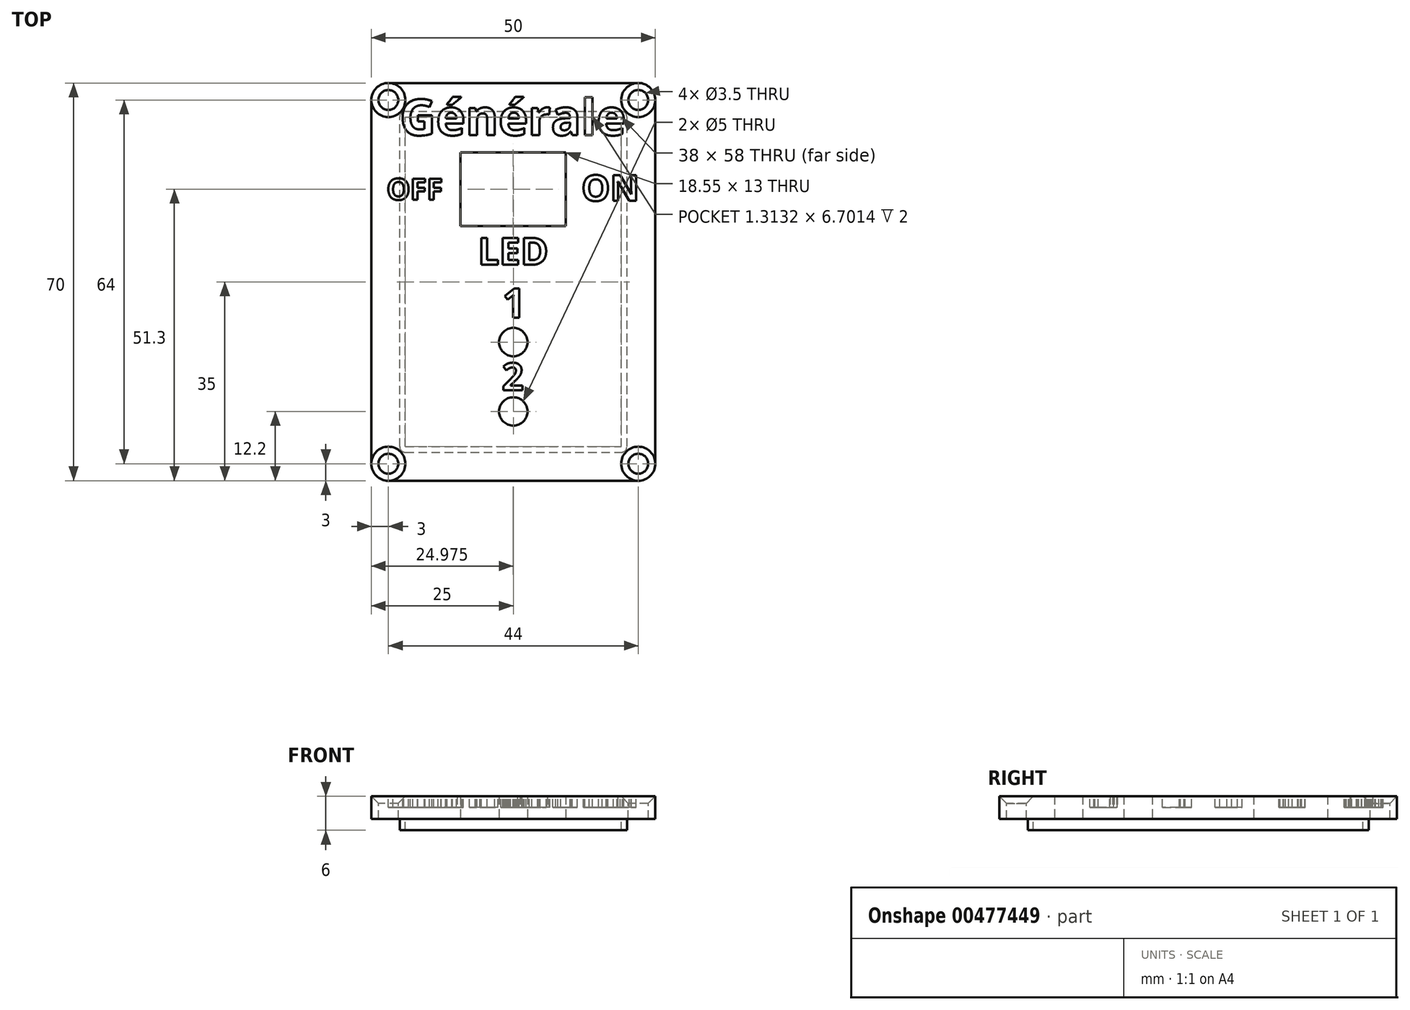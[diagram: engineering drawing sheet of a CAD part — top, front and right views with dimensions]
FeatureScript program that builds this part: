
annotation { "Feature Type Name" : "Feature", "Feature Type Description" : "" }
export const myFeature = defineFeature(function(context is Context, id is Id, definition is map)
    precondition{}
    {
        {
            var Q0;
            Q0=qCreatedBy(makeId("Top.planeOp"),FACE);
            var sketch = newSketch(context, id + "F0", { "sketchPlane" : qUnion([Q0])});
            skLineSegment(sketch, "E0.bottom", {"start": v(-25, 35) * mm, "end": v(25, 35) * mm});
            skLineSegment(sketch, "E0.top", {"start": v(-25, -35) * mm, "end": v(25, -35) * mm});
            skLineSegment(sketch, "E0.left", {"start": v(-25, 35) * mm, "end": v(-25, -35) * mm});
            skLineSegment(sketch, "E0.right", {"start": v(25, 35) * mm, "end": v(25, -35) * mm});
            skLineSegment(sketch, "E1.bottom", {"start": v(-9.3, 22.8) * mm, "end": v(9.25, 22.8) * mm});
            skLineSegment(sketch, "E1.top", {"start": v(-9.3, 9.8) * mm, "end": v(9.25, 9.8) * mm});
            skLineSegment(sketch, "E1.left", {"start": v(-9.3, 22.8) * mm, "end": v(-9.3, 9.8) * mm});
            skLineSegment(sketch, "E1.right", {"start": v(9.25, 22.8) * mm, "end": v(9.25, 9.8) * mm});
            skPoint(sketch, "E2", {"position": v(0, -22.8) * mm});
            skPoint(sketch, "E3", {"position": v(0, -10.6) * mm});
            skSolve(sketch);
        }
        {
            var Q0;
            Q0 = qSketchRegion(id + "F0", true);
            extrude(context, id + "F1", {"entities" : qUnion([Q0]), "depth" : 4 * mm});
        }
        {
            var Q0;
            Q0=sQuery(id+"F0.wireOp",VERTEX,"E3");
            var Q1;
            Q1=sQuery(id+"F0.wireOp",VERTEX,"E2");
            var Q2;
            Q2=makeQuery(id+"F1.opExtrude","SWEPT_BODY",BODY,{"disambiguationData":[OSD([sQuery(id+"F0.wireOp",EDGE,"E0.bottom"),sQuery(id+"F0.wireOp",EDGE,"E0.top"),sQuery(id+"F0.wireOp",EDGE,"E0.left"),sQuery(id+"F0.wireOp",EDGE,"E0.right"),sQuery(id+"F0.wireOp",EDGE,"E1.bottom"),sQuery(id+"F0.wireOp",EDGE,"E1.top"),sQuery(id+"F0.wireOp",EDGE,"E1.left"),sQuery(id+"F0.wireOp",EDGE,"E1.right")])]});
            hole(context, id + "F2", {"style" : HoleStyle.SIMPLE, "endStyle" : HoleEndStyle.THROUGH, "oppositeDirection" : true, "holeDiameter" : 5 * mm, "isTappedThrough" : true, "tappedDepth" : 12.7 * mm, "tapClearance" : 3, "locations" : qUnion([Q0, Q1]), "scope" : qUnion([Q2])});
        }
        {
            var Q0;
            Q0=makeQuery(id+"F1.opExtrude","CAP_FACE",FACE,{"disambiguationData":[OSD([sQuery(id+"F0.wireOp",EDGE,"E0.bottom"),sQuery(id+"F0.wireOp",EDGE,"E0.top"),sQuery(id+"F0.wireOp",EDGE,"E0.left"),sQuery(id+"F0.wireOp",EDGE,"E0.right"),sQuery(id+"F0.wireOp",EDGE,"E1.bottom"),sQuery(id+"F0.wireOp",EDGE,"E1.top"),sQuery(id+"F0.wireOp",EDGE,"E1.left"),sQuery(id+"F0.wireOp",EDGE,"E1.right")])],"isStart":false});
            var sketch = newSketch(context, id + "F3", { "sketchPlane" : qUnion([Q0])});
            skText(sketch, "E4", { "text": "ON", "fontName": "OpenSans-Bold.ttf"});
            skText(sketch, "E5", { "text": "OFF\n", "fontName": "OpenSans-Bold.ttf"});
            skText(sketch, "E6", { "text": "Générale", "fontName": "OpenSans-Bold.ttf"});
            skText(sketch, "E7", { "text": "LED", "fontName": "OpenSans-Bold.ttf"});
            skText(sketch, "E8", { "text": "1", "fontName": "OpenSans-Bold.ttf"});
            skText(sketch, "E9", { "text": "2", "fontName": "OpenSans-Bold.ttf"});
            const initialGuessF3  = {"E4": [0.012, 0.01425, 1, 0, 0.00455], "E5": [-0.0223, 0.01443, 1, 0, 0.00377], "E6": [-0.02, 0.0258, 1, 0, 0.00635], "E7": [-0.00622, 0.003, 1, 0, 0.00478], "E8": [-0.00192, -0.0063, 1, 0, 0.0052], "E9": [-0.00202, -0.01907, 1, 0, 0.00483]};
            skSetInitialGuess(sketch, initialGuessF3);
            skSolve(sketch);
        }
        {
            var Q0;
            Q0 = qSketchRegion(id + "F3", true);
            extrude(context, id + "F4", {"entities" : qUnion([Q0]), "operationType" : NewBodyOperationType.REMOVE, "oppositeDirection" : true, "depth" : 2 * mm});
        }
        {
            var Q0;
            {var subQ0=sQuery(id+"F0.wireOp",EDGE,"E0.bottom");var subQ1=sQuery(id+"F0.wireOp",EDGE,"E0.top");var subQ2=sQuery(id+"F0.wireOp",EDGE,"E0.left");var subQ3=sQuery(id+"F0.wireOp",EDGE,"E0.right");var subQ4=sQuery(id+"F0.wireOp",EDGE,"E1.bottom");var subQ5=sQuery(id+"F0.wireOp",EDGE,"E1.top");var subQ6=sQuery(id+"F0.wireOp",EDGE,"E1.left");var subQ7=sQuery(id+"F0.wireOp",EDGE,"E1.right");Q0=makeQuery(id+"F4.boolean.opBoolean","SPLIT",FACE,{"disambiguationData":[TD([makeQuery(id+"F1.opExtrude","SWEPT_FACE",FACE,{"disambiguationData":[OSD([subQ0])]})])],"derivedFrom":makeQuery(id+"F1.opExtrude","CAP_FACE",FACE,{"disambiguationData":[OSD([subQ0,subQ1,subQ2,subQ3,subQ4,subQ5,subQ6,subQ7])],"isStart":false})});}
            var sketch = newSketch(context, id + "F5", { "sketchPlane" : qUnion([Q0])});
            skPoint(sketch, "E10", {"position": v(-22, 32) * mm});
            skPoint(sketch, "E11", {"position": v(22, 32) * mm});
            skPoint(sketch, "E12", {"position": v(-22, -32) * mm});
            skPoint(sketch, "E13", {"position": v(22, -32) * mm});
            skSolve(sketch);
        }
        {
            var Q0;
            Q0=sQuery(id+"F5.wireOp",VERTEX,"E10");
            var Q1;
            Q1=sQuery(id+"F5.wireOp",VERTEX,"E11");
            var Q2;
            Q2=sQuery(id+"F5.wireOp",VERTEX,"E13");
            var Q3;
            Q3=sQuery(id+"F5.wireOp",VERTEX,"E12");
            var Q4;
            Q4=makeQuery(id+"F1.opExtrude","SWEPT_BODY",BODY,{"disambiguationData":[OSD([sQuery(id+"F0.wireOp",EDGE,"E0.bottom"),sQuery(id+"F0.wireOp",EDGE,"E0.top"),sQuery(id+"F0.wireOp",EDGE,"E0.left"),sQuery(id+"F0.wireOp",EDGE,"E0.right"),sQuery(id+"F0.wireOp",EDGE,"E1.bottom"),sQuery(id+"F0.wireOp",EDGE,"E1.top"),sQuery(id+"F0.wireOp",EDGE,"E1.left"),sQuery(id+"F0.wireOp",EDGE,"E1.right")])]});
            hole(context, id + "F6", {"style" : HoleStyle.C_SINK, "endStyle" : HoleEndStyle.THROUGH, "holeDiameter" : 3.5 * mm, "cSinkDiameter" : 6 * mm, "cSinkAngle" : 90 * degree, "isTappedThrough" : true, "tappedDepth" : 12.7 * mm, "tapClearance" : 3, "locations" : qUnion([Q0, Q1, Q2, Q3]), "scope" : qUnion([Q4])});
        }
        {
            var Q0;
            Q0=makeQuery(id+"F1.opExtrude","SWEPT_EDGE",EDGE,{"disambiguationData":[OSD([sQuery(id+"F0.wireOp",EDGE,"E0.bottom"),sQuery(id+"F0.wireOp",EDGE,"E0.left")])]});
            var Q1;
            Q1=makeQuery(id+"F1.opExtrude","SWEPT_EDGE",EDGE,{"disambiguationData":[OSD([sQuery(id+"F0.wireOp",EDGE,"E0.bottom"),sQuery(id+"F0.wireOp",EDGE,"E0.right")])]});
            var Q2;
            Q2=makeQuery(id+"F1.opExtrude","SWEPT_EDGE",EDGE,{"disambiguationData":[OSD([sQuery(id+"F0.wireOp",EDGE,"E0.top"),sQuery(id+"F0.wireOp",EDGE,"E0.right")])]});
            var Q3;
            Q3=makeQuery(id+"F1.opExtrude","SWEPT_EDGE",EDGE,{"disambiguationData":[OSD([sQuery(id+"F0.wireOp",EDGE,"E0.top"),sQuery(id+"F0.wireOp",EDGE,"E0.left")])]});
            fillet(context, id + "F7", {"entities" : qUnion([Q0, Q1, Q2, Q3]), "radius" : 3 * mm, "tangentPropagation" : true, "allowEdgeOverflow" : false});
        }
        {
            var Q0;
            Q0=makeQuery(id+"F0.imprint","IMPRINT",FACE,{"disambiguationData":[TD([[makeQuery(id+"F0.imprint","IMPRINT",EDGE,{"derivedFrom":sQuery(id+"F0.wireOp",EDGE,"E0.bottom")}),-1.0]])]});
            var sketch = newSketch(context, id + "F8", { "sketchPlane" : qUnion([Q0])});
            skLineSegment(sketch, "E14.bottom", {"start": v(-20, -30) * mm, "end": v(20, -30) * mm});
            skLineSegment(sketch, "E14.top", {"start": v(-20, 30) * mm, "end": v(20, 30) * mm});
            skLineSegment(sketch, "E14.left", {"start": v(-20, -30) * mm, "end": v(-20, 30) * mm});
            skLineSegment(sketch, "E14.right", {"start": v(20, -30) * mm, "end": v(20, 30) * mm});
            skLineSegment(sketch, "E15.bottom", {"start": v(-19, -29) * mm, "end": v(19, -29) * mm});
            skLineSegment(sketch, "E15.top", {"start": v(-19, 29) * mm, "end": v(19, 29) * mm});
            skLineSegment(sketch, "E15.left", {"start": v(-19, -29) * mm, "end": v(-19, 29) * mm});
            skLineSegment(sketch, "E15.right", {"start": v(19, -29) * mm, "end": v(19, 29) * mm});
            skSolve(sketch);
        }
        {
            var Q0;
            Q0=makeQuery(id+"F8.imprint","IMPRINT",FACE,{"disambiguationData":[TD([[makeQuery(id+"F8.imprint","IMPRINT",EDGE,{"derivedFrom":sQuery(id+"F8.wireOp",EDGE,"E14.bottom")}),1.0]])]});
            var Q1;
            Q1=sQuery(id+"F8.wireOp",EDGE,"E15.bottom");
            var Q2;
            Q2=sQuery(id+"F8.wireOp",EDGE,"E14.bottom");
            var Q3;
            Q3=sQuery(id+"F8.wireOp",EDGE,"E14.left");
            var Q4;
            Q4=sQuery(id+"F8.wireOp",EDGE,"E15.left");
            var Q5;
            Q5=sQuery(id+"F8.wireOp",EDGE,"E14.top");
            var Q6;
            Q6=sQuery(id+"F8.wireOp",EDGE,"E15.top");
            var Q7;
            Q7=sQuery(id+"F8.wireOp",EDGE,"E15.right");
            var Q8;
            Q8=sQuery(id+"F8.wireOp",EDGE,"E14.right");
            extrude(context, id + "F9", {"entities" : qUnion([Q0]), "surfaceEntities" : qUnion([Q1, Q2, Q3, Q4, Q5, Q6, Q7, Q8]), "oppositeDirection" : true, "depth" : 2 * mm});
        }
        {
            var Q0;
            Q0=makeQuery(id+"F9.opExtrude","SWEPT_EDGE",EDGE,{"disambiguationData":[OSD([sQuery(id+"F8.wireOp",EDGE,"E14.bottom"),sQuery(id+"F8.wireOp",EDGE,"E14.right")])]});
            var Q1;
            Q1=makeQuery(id+"F9.opExtrude","SWEPT_EDGE",EDGE,{"disambiguationData":[OSD([sQuery(id+"F8.wireOp",EDGE,"E14.bottom"),sQuery(id+"F8.wireOp",EDGE,"E14.left")])]});
            var Q2;
            Q2=makeQuery(id+"F9.opExtrude","SWEPT_EDGE",EDGE,{"disambiguationData":[OSD([sQuery(id+"F8.wireOp",EDGE,"E14.top"),sQuery(id+"F8.wireOp",EDGE,"E14.left")])]});
            var Q3;
            Q3=makeQuery(id+"F9.opExtrude","SWEPT_EDGE",EDGE,{"disambiguationData":[OSD([sQuery(id+"F8.wireOp",EDGE,"E14.top"),sQuery(id+"F8.wireOp",EDGE,"E14.right")])]});
            fillet(context, id + "F10", {"entities" : qUnion([Q0, Q1, Q2, Q3]), "radius" : 1 * mm, "tangentPropagation" : true, "allowEdgeOverflow" : false});
        }
    });
